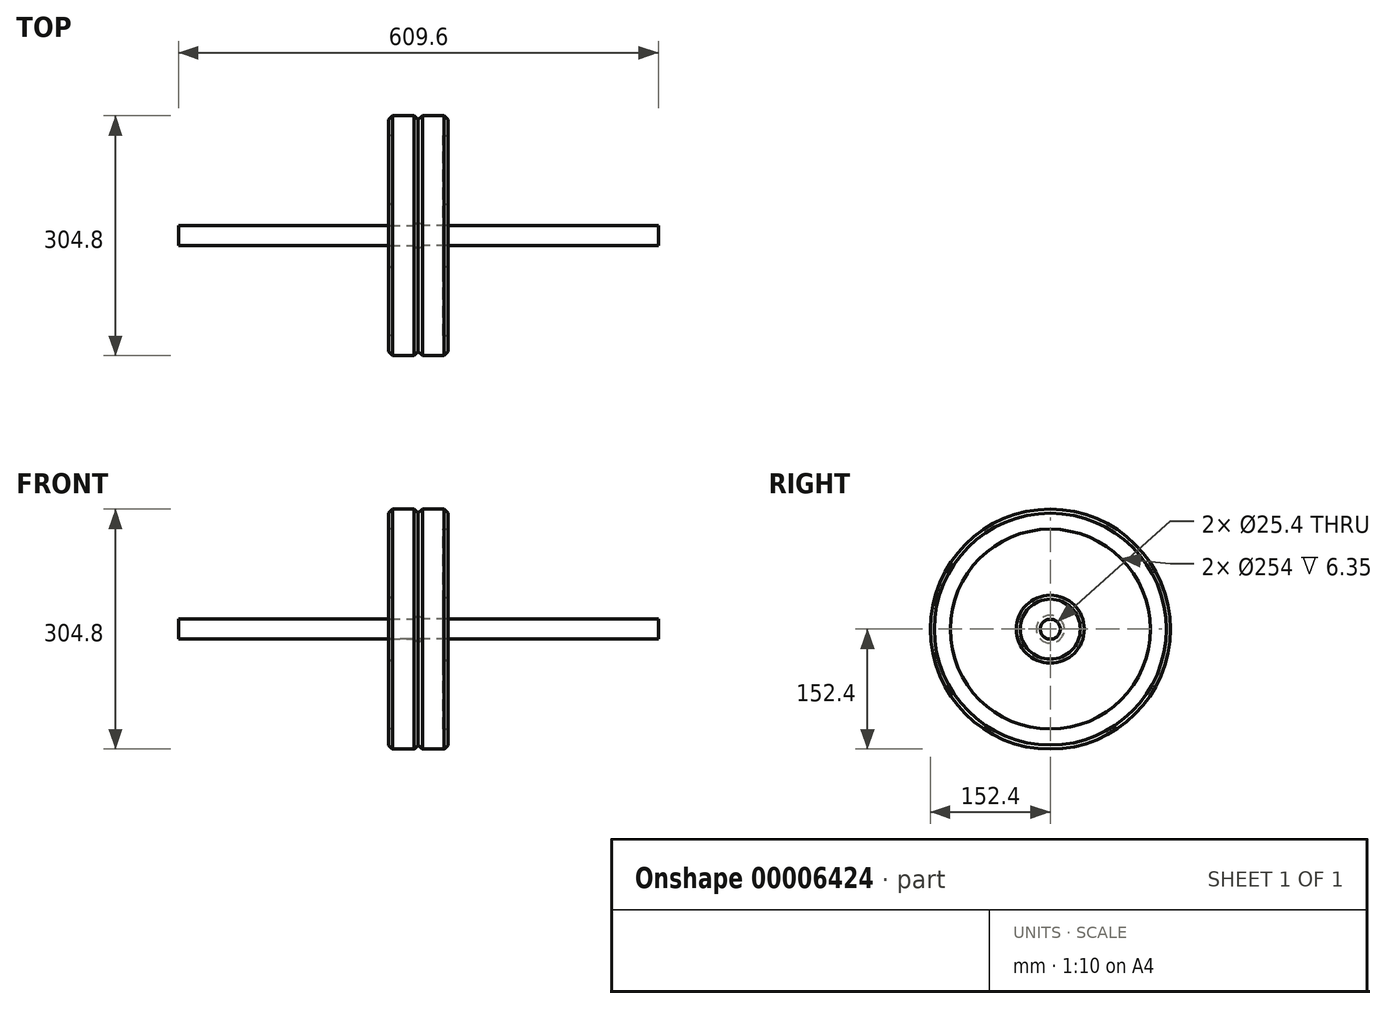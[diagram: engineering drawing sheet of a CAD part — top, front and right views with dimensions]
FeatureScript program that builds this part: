
annotation { "Feature Type Name" : "Feature", "Feature Type Description" : "" }
export const myFeature = defineFeature(function(context is Context, id is Id, definition is map)
    precondition{}
    {
        {
            var Q0;
            Q0=qCreatedBy(makeId("Right.planeOp"),FACE);
            var sketch = newSketch(context, id + "F0", { "sketchPlane" : qUnion([Q0])});
            skCircle(sketch, "E0", {"center": v(0, 0) * mm, "radius": 12.7 * mm});
            skSolve(sketch);
        }
        {
            var Q0;
            Q0 = qSketchRegion(id + "F0", true);
            extrude(context, id + "F1", {"entities" : qUnion([Q0]), "depth" : 304.8 * mm, "hasSecondDirection" : true, "secondDirectionOppositeDirection" : true, "secondDirectionDepth" : 304.8 * mm});
        }
        {
            var Q0;
            Q0=qCreatedBy(makeId("Right.planeOp"),FACE);
            var sketch = newSketch(context, id + "F2", { "sketchPlane" : qUnion([Q0])});
            skCircle(sketch, "E1", {"center": v(0, 0) * mm, "radius": 152.4 * mm});
            skCircle(sketch, "E2", {"center": v(0, 0) * mm, "radius": 12.7 * mm});
            skSolve(sketch);
        }
        {
            var Q0;
            Q0 = qSketchRegion(id + "F2", true);
            extrude(context, id + "F3", {"entities" : qUnion([Q0]), "depth" : 38.1 * mm});
        }
        {
            var Q0;
            Q0=makeQuery(id+"F3.opExtrude","CAP_FACE",FACE,{"disambiguationData":[OSD([sQuery(id+"F2.wireOp",EDGE,"E1"),sQuery(id+"F2.wireOp",EDGE,"E2")])],"isStart":false});
            var sketch = newSketch(context, id + "F4", { "sketchPlane" : qUnion([Q0])});
            skCircle(sketch, "E3.0", {"center": v(0, 0) * mm, "radius": 127 * mm});
            skCircle(sketch, "E4.0", {"center": v(0, 0) * mm, "radius": 38.1 * mm});
            skSolve(sketch);
        }
        {
            var Q0;
            Q0=makeQuery(id+"F4.imprint","IMPRINT",FACE,{"disambiguationData":[TD([[makeQuery(id+"F4.imprint","IMPRINT",EDGE,{"derivedFrom":sQuery(id+"F4.wireOp",EDGE,"E3.0")}),1.0]])]});
            extrude(context, id + "F5", {"entities" : qUnion([Q0]), "operationType" : NewBodyOperationType.REMOVE, "oppositeDirection" : true, "depth" : 6.35 * mm});
        }
        {
            var Q0;
            Q0=makeQuery(id+"F5.boolean.opBoolean","COPY",EDGE,{"derivedFrom":makeQuery(id+"F5.opExtrude","CAP_EDGE",EDGE,{"disambiguationData":[OSD([sQuery(id+"F4.wireOp",EDGE,"E3.0")])],"isStart":true})});
            var Q1;
            Q1=makeQuery(id+"F5.boolean.opBoolean","COPY",EDGE,{"derivedFrom":makeQuery(id+"F5.opExtrude","CAP_EDGE",EDGE,{"disambiguationData":[OSD([sQuery(id+"F4.wireOp",EDGE,"E4.0")])],"isStart":false})});
            var Q2;
            Q2=makeQuery(id+"F3.opExtrude","CAP_EDGE",EDGE,{"disambiguationData":[OSD([sQuery(id+"F2.wireOp",EDGE,"E1")])],"isStart":false});
            var Q3;
            Q3=makeQuery(id+"F3.opExtrude","CAP_FACE",FACE,{"disambiguationData":[OSD([sQuery(id+"F2.wireOp",EDGE,"E1"),sQuery(id+"F2.wireOp",EDGE,"E2")])],"isStart":true});
            chamfer(context, id + "F6", {"entities" : qUnion([Q0, Q1, Q2, Q3]), "width" : 5.08 * mm, "tangentPropagation" : true});
        }
        {
            var Q0;
            Q0=makeQuery(id+"F3.opExtrude","SWEPT_BODY",BODY,{"disambiguationData":[OSD([sQuery(id+"F2.wireOp",EDGE,"E1"),sQuery(id+"F2.wireOp",EDGE,"E2")])]});
            var Q1;
            Q1=makeQuery(id+"F3.opExtrude","CAP_FACE",FACE,{"disambiguationData":[OSD([sQuery(id+"F2.wireOp",EDGE,"E1"),sQuery(id+"F2.wireOp",EDGE,"E2")])],"isStart":true});
            mirror(context, id + "F7", {"entities" : qUnion([Q0]), "mirrorPlane" : qUnion([Q1])});
        }
    });
